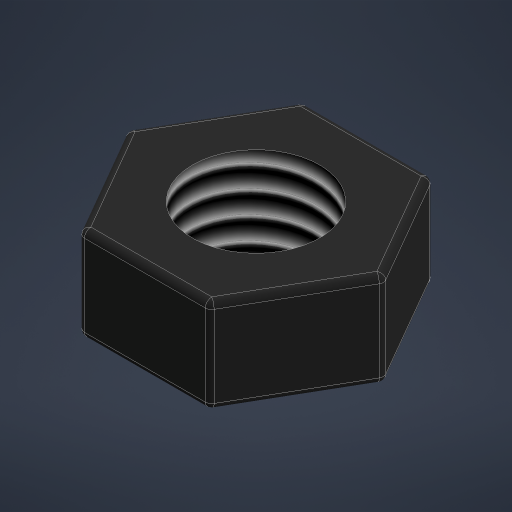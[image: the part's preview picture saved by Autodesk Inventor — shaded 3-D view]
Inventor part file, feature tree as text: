
AUTODESK INVENTOR PART (.ipt)
format: ipt  version: 2024 (Build 280153000, 153)  size: 231,424 bytes
history: native  units: mm
features: extrude x1, fillet x1, thread x1, sketch x1
ambient origin geometry x8: Origin, YZ Plane, XZ Plane, XY Plane, X Axis, Y Axis, Z Axis, Center Point
bodies: Solid1 (feature_tree)
feature tree (4):
  extrude  "Extrusion1"  Depth=0.2mm
  fillet  "Fillet1"  Radius=2.93mm
  thread  "Thread1"  [1 undecoded]
  sketch  "Sketch1"  dims[d0=6.9mm d1=3.94mm d2=2.93mm d3=0.0mm d4=0.2mm d5=3.8mm d6=0.0mm]
note: 1 required parameter value undecoded (feature->parameter linkage not recoverable at this tier; creation-order binding heuristic only, values carry confidence <= 0.55)
